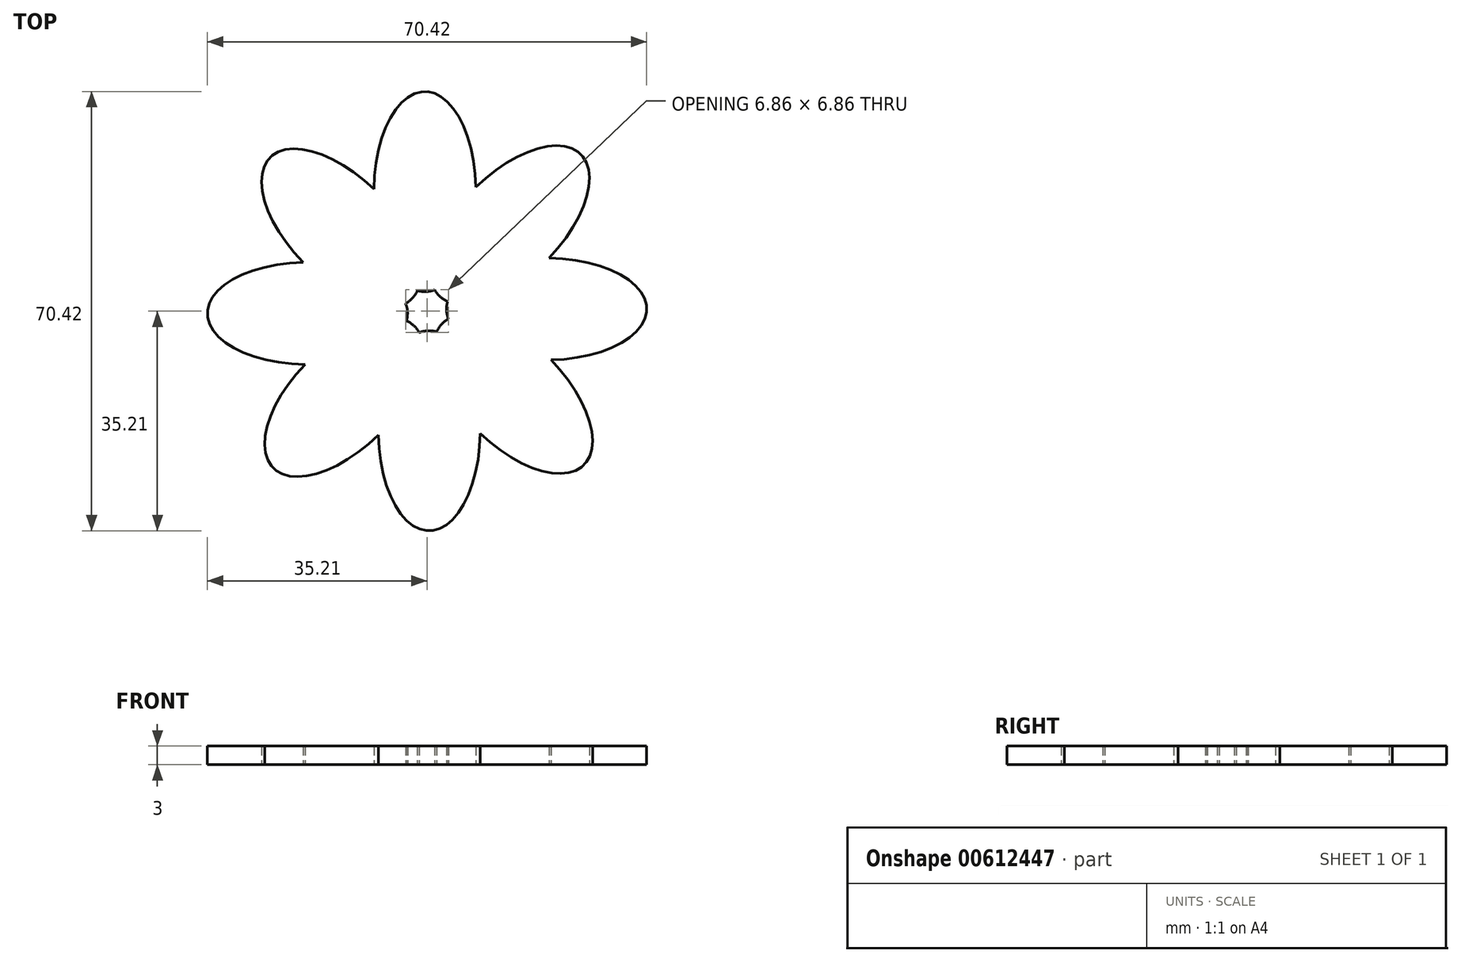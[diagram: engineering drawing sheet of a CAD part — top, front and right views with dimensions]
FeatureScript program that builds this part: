
annotation { "Feature Type Name" : "Feature", "Feature Type Description" : "" }
export const myFeature = defineFeature(function(context is Context, id is Id, definition is map)
    precondition{}
    {
        {
            var Q0;
            Q0=qCreatedBy(makeId("Top.planeOp"),FACE);
            var sketch = newSketch(context, id + "F0", { "sketchPlane" : qUnion([Q0])});
            skLineSegment(sketch, "E0.bottom", {"start": v(0, 75.02) * mm, "end": v(75.36, 75.02) * mm});
            skLineSegment(sketch, "E0.top", {"start": v(0, 0) * mm, "end": v(75.36, 0) * mm});
            skLineSegment(sketch, "E0.left", {"start": v(0, 75.02) * mm, "end": v(0, 0) * mm});
            skLineSegment(sketch, "E0.right", {"start": v(75.36, 75.02) * mm, "end": v(75.36, 0) * mm});
            skSolve(sketch);
        }
        {
            var Q0;
            Q0=makeQuery(id+"F0.imprint","IMPRINT",FACE,{"disambiguationData":[TD([[makeQuery(id+"F0.imprint","IMPRINT",EDGE,{"derivedFrom":sQuery(id+"F0.wireOp",EDGE,"E0.bottom")}),-1.0]])]});
            var sketch = newSketch(context, id + "F1", { "sketchPlane" : qUnion([Q0])});
            skLineSegment(sketch, "E1", {"start": v(0, 74.8) * mm, "end": v(76.04, 0) * mm});
            skSolve(sketch);
        }
        {
            var Q0;
            Q0=makeQuery(id+"F0.imprint","IMPRINT",FACE,{"disambiguationData":[TD([[makeQuery(id+"F0.imprint","IMPRINT",EDGE,{"derivedFrom":sQuery(id+"F0.wireOp",EDGE,"E0.bottom")}),-1.0]])]});
            var sketch = newSketch(context, id + "F2", { "sketchPlane" : qUnion([Q0])});
            skEllipticalArc(sketch, "E2", {});
            skEllipticalArc(sketch, "E3.1.0", {});
            skEllipticalArc(sketch, "E3.2.0", {});
            skPoint(sketch, "E3.center", {"position": v(38.2, 38) * mm});
            skEllipticalArc(sketch, "E4.1.3.0", {});
            skEllipticalArc(sketch, "E4.1.4.0", {});
            skEllipticalArc(sketch, "E4.1.5.0", {});
            skEllipticalArc(sketch, "E4.1.6.0", {});
            skEllipticalArc(sketch, "E4.1.7.0", {});
            skEllipticalArc(sketch, "E5.trimOffspring", {});
            skEllipticalArc(sketch, "E6.trimOffspring", {});
            skEllipticalArc(sketch, "E7.trimOffspring", {});
            skEllipticalArc(sketch, "E8.trimOffspring", {});
            skEllipticalArc(sketch, "E9.trimOffspring", {});
            skEllipticalArc(sketch, "E10.trimOffspring", {});
            skEllipticalArc(sketch, "E11.trimOffspring", {});
            skEllipticalArc(sketch, "E12.trimOffspring", {});
            const initialGuessF2  = {"E2": [0.03784971311688423, 0.05717001482844353, 0, 1, 0.016043763607740402, 0.008174689674884364, 2.994042683290469, 3.3369260654056747], "E3.1.0": [0.02439706228894905, 0.05130755725022721, -0.7071067811865475, 0.7071067811865477, 0.016043763607740402, 0.008174689674884364, 4.755974007966083, 1.5454422049560206], "E3.2.0": [0.01902998517155649, 0.037649713116884226, -1, 0, 0.016043763607740402, 0.008174689674884364, 2.994042683290469, 3.3369260654056747], "E4.1.3.0": [0.024892442749772772, 0.024197062288949054, -0.7071067811865476, -0.7071067811865475, 0.016043763607740402, 0.008174689674884364, 2.9940426832904676, 3.3369260654056747], "E4.1.4.0": [0.03855028688311576, 0.018829985171556464, 0, -1, 0.016043763607740402, 0.008174689674884364, 2.9940426832904667, 3.3369260654056734], "E4.1.5.0": [0.052002937711050946, 0.024692442749772753, 0.7071067811865475, -0.7071067811865477, 0.016043763607740402, 0.008174689674884364, 2.994042683290467, 3.336926065405674], "E4.1.6.0": [0.057370014828443526, 0.03835028688311576, 1, 0, 0.016043763607740402, 0.008174689674884364, 2.9940426832904667, 3.336926065405677], "E4.1.7.0": [0.05150755725022724, 0.05180293771105095, 0.7071067811865477, 0.7071067811865474, 0.016043763607740402, 0.008174689674884364, 2.9940426832904676, 3.3369260654056734], "E5.trimOffspring": [0.03784971311688423, 0.05717001482844353, 0, 1, 0.016043763607740402, 0.008174689674884364, 4.755974007966083, 1.5454422049560232], "E6.trimOffspring": [0.05150755725022724, 0.05180293771105095, 0.7071067811865477, 0.7071067811865474, 0.016043763607740402, 0.008174689674884364, 4.755974007966082, 1.5454422049560228], "E7.trimOffspring": [0.057370014828443526, 0.03835028688311576, 1, 0, 0.016043763607740402, 0.008174689674884364, 4.755974007966083, 1.5454422049560221], "E8.trimOffspring": [0.052002937711050946, 0.024692442749772753, 0.7071067811865475, -0.7071067811865477, 0.016043763607740402, 0.008174689674884364, 4.755974007966082, 1.5454422049560226], "E9.trimOffspring": [0.03855028688311576, 0.018829985171556464, 0, -1, 0.016043763607740402, 0.008174689674884364, 4.755974007966083, 1.5454422049560226], "E10.trimOffspring": [0.024892442749772772, 0.024197062288949054, -0.7071067811865476, -0.7071067811865475, 0.016043763607740402, 0.008174689674884364, 4.755974007966083, 1.5454422049560208], "E11.trimOffspring": [0.02439706228894905, 0.05130755725022721, -0.7071067811865475, 0.7071067811865477, 0.016043763607740402, 0.008174689674884364, 2.9940426832904716, 3.3369260654056774], "E12.trimOffspring": [0.01902998517155649, 0.037649713116884226, -1, 0, 0.016043763607740402, 0.008174689674884364, 4.755974007966085, 1.5454422049560208]};
            skSetInitialGuess(sketch, initialGuessF2);
            skSolve(sketch);
        }
        {
            var Q0;
            Q0 = qSketchRegion(id + "F2", true);
            extrude(context, id + "F3", {"entities" : qUnion([Q0]), "depth" : 3 * mm, "offsetDistance" : 25 * mm});
        }
    });
